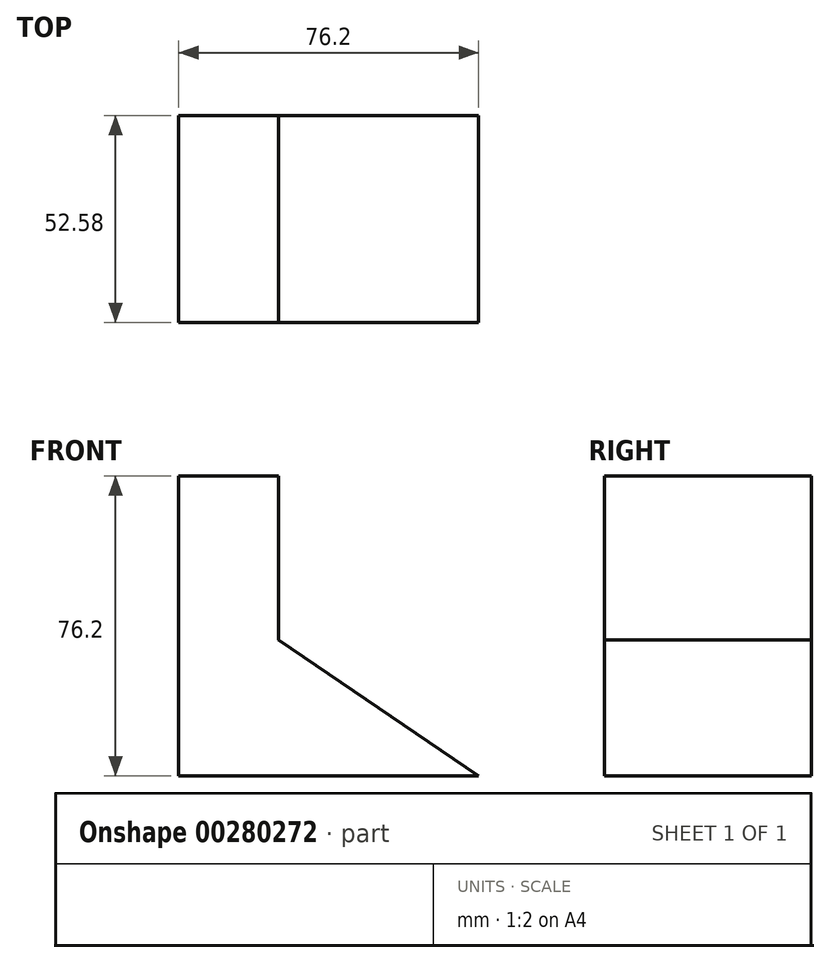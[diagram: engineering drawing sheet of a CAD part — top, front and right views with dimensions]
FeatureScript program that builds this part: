
annotation { "Feature Type Name" : "Feature", "Feature Type Description" : "" }
export const myFeature = defineFeature(function(context is Context, id is Id, definition is map)
    precondition{}
    {
        {
            var Q0;
            Q0=qCreatedBy(makeId("Front.planeOp"),FACE);
            var sketch = newSketch(context, id + "F0", { "sketchPlane" : qUnion([Q0])});
            skLineSegment(sketch, "E0", {"start": v(-76.2, 76.2) * mm, "end": v(-76.2, 0) * mm});
            skLineSegment(sketch, "E1", {"start": v(-76.2, 0) * mm, "end": v(0, 0) * mm});
            skLineSegment(sketch, "E2", {"start": v(-76.2, 76.2) * mm, "end": v(-50.8, 76.2) * mm});
            skLineSegment(sketch, "E3", {"start": v(-50.8, 76.2) * mm, "end": v(-50.8, 34.59) * mm});
            skLineSegment(sketch, "E4", {"start": v(-50.8, 34.59) * mm, "end": v(0, 0) * mm});
            skSolve(sketch);
        }
        {
            var Q0;
            Q0 = qSketchRegion(id + "F0", true);
            extrude(context, id + "F1", {"entities" : qUnion([Q0]), "depth" : 52.58 * mm});
        }
    });
